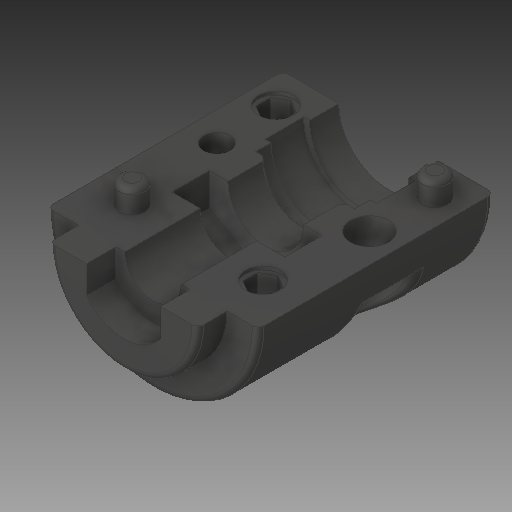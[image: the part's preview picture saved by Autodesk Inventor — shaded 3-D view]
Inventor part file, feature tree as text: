
AUTODESK INVENTOR PART (.ipt)
format: ipt  version: 2017 (Build 210142000, 142)  size: 257,536 bytes
history: native  units: in
note: dims shown in document units (in); Inventor stores cm internally (conversion verified against a paired STEP export)
features: fillet x1
ambient origin geometry x8: Origin, YZ Plane, XZ Plane, XY Plane, X Axis, Y Axis, Z Axis, Center Point
bodies: Solid1 (feature_tree)
feature tree (1):
  fillet  "Fillet1"  [1 undecoded]
note: 1 required parameter value undecoded (feature->parameter linkage not recoverable at this tier; creation-order binding heuristic only, values carry confidence <= 0.55)
